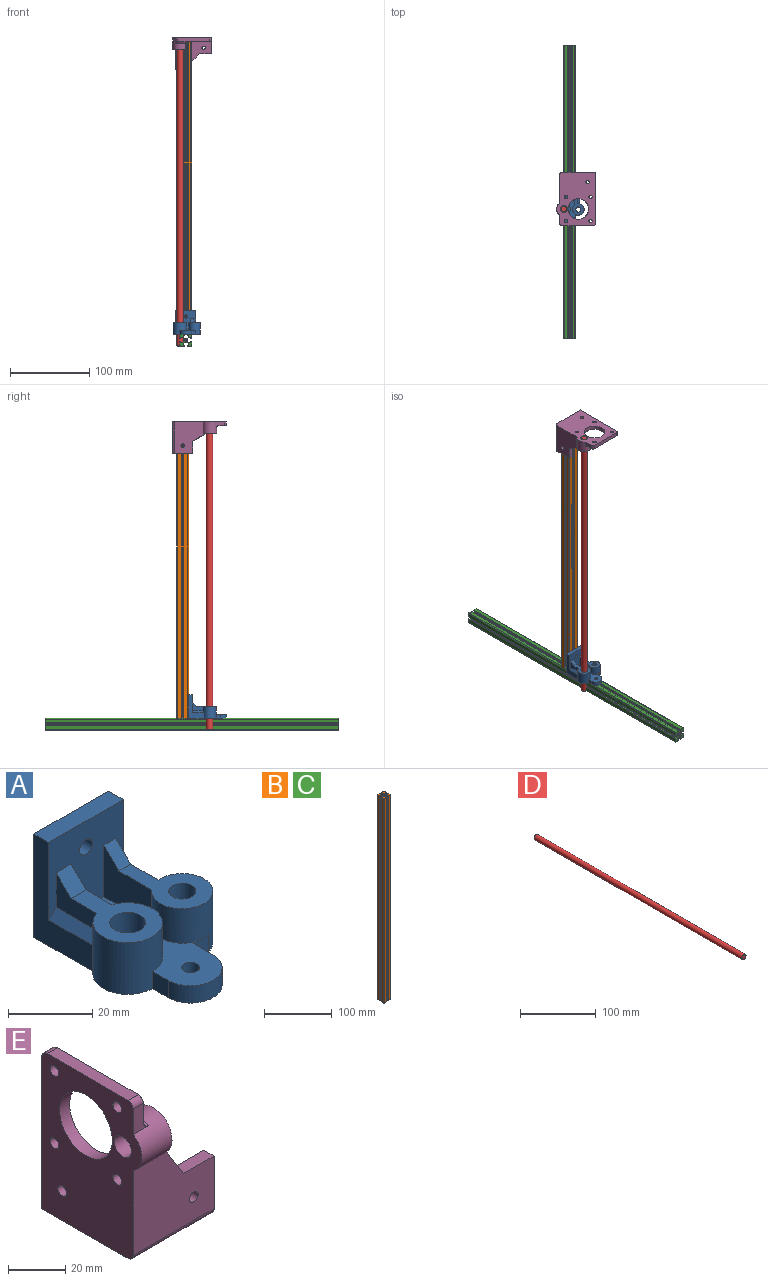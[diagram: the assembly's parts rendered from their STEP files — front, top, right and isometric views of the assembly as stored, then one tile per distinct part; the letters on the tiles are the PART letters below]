
ASSEMBLY  parts=5 mates=10
PART A: 29 faces, bbox 33.8x47.6x30 mm
  f0: plane 25x25mm, normal (0,-1,0), area 457.1mm2, adj f2,f7,f9,f16,f20,f21,f22,f23
  f1: cylinder r=8.25mm len=16.5mm, axis (0,0,-1), area 559.8mm2, adj f2,f9,f14,f15,f17,f21,f22,f26
  f2: plane 42.6x16.6mm, normal (0,0,1), area 386.9mm2, adj f0,f1,f3,f4,f5,f6,f10,f11
  f3: cylinder r=7.5mm len=15mm, axis (0,0,-1), area 117.8mm2, adj f2,f4,f14,f15
  f4: plane 6.55x5mm, normal (1,0,0), area 32.8mm2, adj f2,f3,f5,f15
  f5: plane 5x5mm, normal (0,-1,0), area 25mm2, adj f2,f4,f6,f15,f18
  f6: cylinder r=7.25mm len=15mm, axis (0,0,-1), area 498.4mm2, adj f2,f5,f7,f15,f18,f19,f23,f24
  f7: plane 30x19.45mm, normal (1,0,0), area 258.4mm2, adj f0,f6,f8,f15,f16,f25
  f8: plane 30x25mm, normal (0,1,0), area 735.8mm2, adj f7,f9,f15,f16,f20
  f9: plane 30x19.94mm, normal (-1,0,0), area 262mm2, adj f0,f1,f8,f15,f16,f26
  f10: cylinder r=2.12mm len=5mm, axis (0,0,-1), area 66.8mm2, adj f2,f15
  f11: cylinder r=2.12mm len=5mm, axis (0,0,-1), area 66.8mm2, adj f2,f15
  f12: cylinder r=4.25mm len=15mm, axis (0,0,-1), area 400.6mm2, adj f15,f17
  f13: cylinder r=3.25mm len=15mm, axis (0,0,-1), area 306.3mm2, adj f15,f19
  f14: plane 5.35x5mm, normal (-1,0,0), area 26.7mm2, adj f1,f2,f3,f15
  f15: plane 47.6x33.8mm, normal (0,0,-1), area 998.3mm2, adj f1,f3,f4,f5,f6,f7,f8,f9
  f16: plane 25x5mm, normal (0,0,1), area 125mm2, adj f0,f7,f8,f9
  f17: plane 24.75x16.5mm, normal (0,0,1), area 199mm2, adj f1,f12,f21,f22,f28
  f18: plane 3.4x0.2mm, normal (0,0,-1), area 0.5mm2, adj f5,f6
  f19: plane 23.75x14.5mm, normal (0,0,1), area 171.7mm2, adj f6,f13,f23,f24,f27
  f20: cylinder r=2.12mm len=5mm, axis (0,-1,0), area 66.8mm2, adj f0,f8
  f21: plane 15x13.64mm, normal (1,0,0), area 148.9mm2, adj f0,f1,f2,f17,f28
  f22: plane 13.64x10mm, normal (-1,0,0), area 80.7mm2, adj f0,f1,f17,f26,f28
  f23: plane 14.29x10mm, normal (1,0,0), area 84mm2, adj f0,f6,f19,f25,f27
  f24: plane 16.07x15mm, normal (-1,0,0), area 173.2mm2, adj f0,f2,f6,f19,f27
  f25: plane 14.47x2.52mm, normal (0.71,0,0.71), area 50.6mm2, adj f0,f6,f7,f23
  f26: plane 14.94x2.5mm, normal (-0.71,0,0.71), area 50.2mm2, adj f0,f1,f9,f22
  f27: plane 5x5mm, normal (0,-0.71,0.71), area 28.3mm2, adj f0,f19,f23,f24
  f28: plane 5x5mm, normal (0,-0.71,0.71), area 35.4mm2, adj f0,f17,f21,f22
PART B: 63 faces, bbox 15x15x370 mm
  f0: plane 370x4.8mm, normal (0,1,0), area 1776mm2, adj f1,f60,f61,f62
  f1: cylinder r=1mm len=370mm, axis (0,0,-1), area 581.2mm2, adj f0,f2,f61,f62
  f2: plane 370x4.8mm, normal (-1,0,0), area 1776mm2, adj f1,f3,f61,f62
  f3: plane 370x1.1mm, normal (0,-1,0), area 407mm2, adj f2,f4,f61,f62
  f4: plane 370x1.15mm, normal (1,0,0), area 425.5mm2, adj f3,f5,f61,f62
  f5: plane 370x2.6mm, normal (0,-1,0), area 962mm2, adj f4,f6,f61,f62
  f6: plane 370x1.15mm, normal (-0.75,-0.66,0), area 563.9mm2, adj f5,f7,f61,f62
  f7: plane 370x1.18mm, normal (-1,0,0), area 436.7mm2, adj f6,f8,f61,f62
  f8: plane 370x0.52mm, normal (-0.87,-0.5,0), area 222mm2, adj f7,f9,f61,f62
  f9: plane 370x0.52mm, normal (-0.87,0.5,0), area 222mm2, adj f8,f10,f61,f62
  f10: plane 370x1.18mm, normal (-1,0,0), area 436.7mm2, adj f9,f11,f61,f62
  f11: plane 370x1.15mm, normal (-0.75,0.66,0), area 563.9mm2, adj f10,f12,f61,f62
  f12: plane 370x2.6mm, normal (0,1,0), area 962mm2, adj f11,f13,f61,f62
  f13: plane 370x1.15mm, normal (1,0,0), area 425.5mm2, adj f12,f14,f61,f62
  f14: plane 370x1.1mm, normal (0,1,0), area 407mm2, adj f13,f15,f61,f62
  f15: plane 370x4.8mm, normal (-1,0,0), area 1776mm2, adj f14,f16,f61,f62
  f16: cylinder r=1mm len=370mm, axis (0,0,-1), area 581.2mm2, adj f15,f17,f61,f62
  f17: plane 370x4.8mm, normal (0,-1,0), area 1776mm2, adj f16,f18,f61,f62
  f18: plane 370x1.1mm, normal (1,0,0), area 407mm2, adj f17,f19,f61,f62
  f19: plane 370x1.15mm, normal (0,1,0), area 425.5mm2, adj f18,f20,f61,f62
  f20: plane 370x2.6mm, normal (1,0,0), area 962mm2, adj f19,f21,f61,f62
  f21: plane 370x1.15mm, normal (0.66,-0.75,0), area 563.9mm2, adj f20,f22,f61,f62
  f22: plane 370x1.18mm, normal (0,-1,0), area 436.7mm2, adj f21,f23,f61,f62
  f23: plane 370x0.52mm, normal (0.5,-0.87,0), area 222mm2, adj f22,f24,f61,f62
  f24: plane 370x0.52mm, normal (-0.5,-0.87,0), area 222mm2, adj f23,f25,f61,f62
  f25: plane 370x1.18mm, normal (0,-1,0), area 436.7mm2, adj f24,f26,f61,f62
  f26: plane 370x1.15mm, normal (-0.66,-0.75,0), area 563.9mm2, adj f25,f27,f61,f62
  f27: plane 370x2.6mm, normal (-1,0,0), area 962mm2, adj f26,f28,f61,f62
  f28: plane 370x1.15mm, normal (0,1,0), area 425.5mm2, adj f27,f29,f61,f62
  f29: plane 370x1.1mm, normal (-1,0,0), area 407mm2, adj f28,f30,f61,f62
  f30: plane 370x4.8mm, normal (0,-1,0), area 1776mm2, adj f29,f31,f61,f62
  f31: cylinder r=1mm len=370mm, axis (0,0,-1), area 581.2mm2, adj f30,f32,f61,f62
  f32: plane 370x4.8mm, normal (1,0,0), area 1776mm2, adj f31,f33,f61,f62
  f33: plane 370x1.1mm, normal (0,1,0), area 407mm2, adj f32,f34,f61,f62
  f34: plane 370x1.15mm, normal (-1,0,0), area 425.5mm2, adj f33,f35,f61,f62
  f35: plane 370x2.6mm, normal (0,1,0), area 962mm2, adj f34,f36,f61,f62
  f36: plane 370x1.15mm, normal (0.75,0.66,0), area 563.9mm2, adj f35,f37,f61,f62
  f37: plane 370x1.18mm, normal (1,0,0), area 436.7mm2, adj f36,f38,f61,f62
  f38: plane 370x0.52mm, normal (0.87,0.5,0), area 222mm2, adj f37,f39,f61,f62
  f39: plane 370x0.52mm, normal (0.87,-0.5,0), area 222mm2, adj f38,f40,f61,f62
  f40: plane 370x1.18mm, normal (1,0,0), area 436.7mm2, adj f39,f41,f61,f62
  f41: plane 370x1.15mm, normal (0.75,-0.66,0), area 563.9mm2, adj f40,f42,f61,f62
  f42: plane 370x2.6mm, normal (0,-1,0), area 962mm2, adj f41,f43,f61,f62
  f43: plane 370x1.15mm, normal (-1,0,0), area 425.5mm2, adj f42,f44,f61,f62
  f44: plane 370x1.1mm, normal (0,-1,0), area 407mm2, adj f43,f45,f61,f62
  f45: plane 370x4.8mm, normal (1,0,0), area 1776mm2, adj f44,f46,f61,f62
  f46: cylinder r=1mm len=370mm, axis (0,0,-1), area 581.2mm2, adj f45,f47,f61,f62
  f47: plane 370x4.8mm, normal (0,1,0), area 1776mm2, adj f46,f48,f61,f62
  f48: plane 370x1.1mm, normal (-1,0,0), area 407mm2, adj f47,f49,f61,f62
  f49: plane 370x1.15mm, normal (0,-1,0), area 425.5mm2, adj f48,f50,f61,f62
  f50: plane 370x2.6mm, normal (-1,0,0), area 962mm2, adj f49,f51,f61,f62
  f51: plane 370x1.15mm, normal (-0.66,0.75,0), area 563.9mm2, adj f50,f52,f61,f62
  f52: plane 370x1.18mm, normal (0,1,0), area 436.7mm2, adj f51,f53,f61,f62
  f53: plane 370x0.52mm, normal (-0.5,0.87,0), area 222mm2, adj f52,f54,f61,f62
  f54: plane 370x0.52mm, normal (0.5,0.87,0), area 222mm2, adj f53,f55,f61,f62
  f55: plane 370x1.18mm, normal (0,1,0), area 436.7mm2, adj f54,f56,f61,f62
  f56: plane 370x1.15mm, normal (0.66,0.75,0), area 563.9mm2, adj f55,f57,f61,f62
  f57: plane 370x2.6mm, normal (1,0,0), area 962mm2, adj f56,f58,f61,f62
  f58: plane 370x1.15mm, normal (0,-1,0), area 425.5mm2, adj f57,f60,f61,f62
  f59: cylinder r=1.25mm len=370mm, axis (0,0,-1), area 2906mm2, adj f61,f62
  f60: plane 370x1.1mm, normal (1,0,0), area 407mm2, adj f0,f58,f61,f62
  f61: plane 15x15mm, normal (0,0,1), area 126.2mm2, adj f0,f1,f2,f3,f4,f5,f6,f7
  f62: plane 15x15mm, normal (0,0,-1), area 126.2mm2, adj f0,f1,f2,f3,f4,f5,f6,f7
PART C: same geometry as B
PART D: 5 faces, bbox 8x390x8 mm
  f0: cylinder r=4mm len=389mm, axis (0,1,0), area 9776.6mm2, adj f3,f4
  f1: plane 7x7mm, normal (0,-1,0), area 38.5mm2, adj f4
  f2: plane 7x7mm, normal (0,1,0), area 38.5mm2, adj f3
  f3: cone r=4mm half-angle=45deg, axis (0,-1,0), area 16.7mm2, adj f0,f2
  f4: cone r=3.5mm half-angle=45deg, axis (0,1,0), area 16.7mm2, adj f0,f1
PART E: 36 faces, bbox 40x49.3x67.6 mm
  f0: plane 10.82x7.5mm, normal (0,-1,0), area 55.7mm2, adj f4,f11,f28,f30,f35
  f1: plane 35x23.9mm, normal (0,1,0), area 759.1mm2, adj f3,f4,f7,f15,f18,f31,f32
  f2: plane 14.94x7.9mm, normal (0,1,0), area 59.7mm2, adj f4,f5,f6,f31,f32,f34
  f3: plane 15x5mm, normal (0,0,1), area 75mm2, adj f1,f12,f15,f31
  f4: plane 62.6x45mm, normal (1,0,0), area 1806.8mm2, adj f0,f1,f2,f7,f10,f19,f20,f21
  f5: cylinder r=9.25mm len=7.5mm, axis (-1,0,0), area 58.1mm2, adj f2,f6,f23,f34
  f6: plane 18.5x16.12mm, normal (1,0,0), area 148.2mm2, adj f2,f5,f12,f23,f30,f31,f33
  f7: plane 40x35mm, normal (0,0,1), area 921.6mm2, adj f1,f4,f8,f9,f10,f13,f14,f15
  f8: plane 10x5mm, normal (0,1,0), area 50mm2, adj f7,f15,f16,f17
  f9: plane 15x5mm, normal (1,0,0), area 75mm2, adj f7,f10,f16,f17
  f10: plane 65.1x20mm, normal (0,1,0), area 400.5mm2, adj f4,f7,f9,f11,f16,f27
  f11: plane 67.6x49.25mm, normal (-1,0,0), area 2426mm2, adj f0,f10,f12,f16,f19,f20,f21,f22
  f12: plane 40x38.5mm, normal (0,-1,0), area 1171.6mm2, adj f3,f6,f11,f15,f18,f29,f30,f31
  f13: cylinder r=2.12mm len=5mm, axis (0,0,-1), area 66.8mm2, adj f7,f16
  f14: cylinder r=2.12mm len=5mm, axis (0,0,-1), area 66.8mm2, adj f7,f16
  f15: plane 25x20mm, normal (1,0,0), area 198.7mm2, adj f1,f3,f7,f8,f12,f16,f29
  f16: plane 42.5x40mm, normal (0,0,-1), area 1221.6mm2, adj f8,f9,f10,f11,f13,f14,f15,f17
  f17: plane 10x10mm, normal (0.71,0.71,0), area 70.7mm2, adj f7,f8,f9,f16
  f18: cylinder r=2.12mm len=5mm, axis (0,-1,0), area 66.8mm2, adj f1,f12
  f19: cylinder r=2.12mm len=5mm, axis (-1,0,0), area 66.8mm2, adj f4,f11
  f20: plane 40x5mm, normal (0,0,1), area 200mm2, adj f4,f11,f27,f28
  f21: cylinder r=2.12mm len=5mm, axis (-1,0,0), area 66.8mm2, adj f4,f11
  f22: cylinder r=4.25mm len=14.5mm, axis (-1,0,0), area 387.2mm2, adj f11,f33
  f23: cylinder r=13mm len=26mm, axis (-1,0,0), area 540.3mm2, adj f4,f5,f6,f11,f30,f34,f35
  f24: cylinder r=2.12mm len=5mm, axis (-1,0,0), area 66.8mm2, adj f4,f11
  f25: cylinder r=2.12mm len=5mm, axis (-1,0,0), area 66.8mm2, adj f4,f11
  f26: cylinder r=2.12mm len=5mm, axis (-1,0,0), area 66.8mm2, adj f4,f11
  f27: cylinder r=2.5mm len=5mm, axis (1,0,0), area 19.6mm2, adj f4,f10,f11,f20
  f28: cylinder r=2.5mm len=5mm, axis (-1,0,0), area 19.6mm2, adj f0,f4,f11,f20
  f29: cylinder r=2.5mm len=40mm, axis (1,0,0), area 157.1mm2, adj f11,f12,f15,f16
  f30: cylinder r=9.25mm len=17.03mm, axis (-1,0,0), area 375.1mm2, adj f0,f6,f11,f12,f23,f35
  f31: plane 16x10mm, normal (0.85,0,0.53), area 92mm2, adj f1,f2,f3,f6,f12,f32
  f32: cylinder r=3.5mm len=17.56mm, axis (-1,0,0), area 73.2mm2, adj f1,f2,f4,f31
  f33: cone r=4.25mm half-angle=45deg, axis (1,0,0), area 20mm2, adj f6,f22
  f34: torus R=11.75mm, axis (1,0,0), area 32.4mm2, adj f2,f4,f5,f23
  f35: torus R=11.75mm, axis (1,0,0), area 52.9mm2, adj f0,f4,f23,f30
PLACE A rot(axis=(-1,0,0),0deg) t=(-117.36,-78.12,35.78)mm
PLACE B rot(axis=(1,0,0),0deg) t=(-117.36,-44.12,220.78)mm
PLACE C rot(axis=(-1,0,0),90deg) t=(-117.36,-55.94,28.28)mm
PLACE D rot(axis=(1,0,0),90deg) t=(-124.86,-78.12,215.78)mm
PLACE E rot(axis=(0.58,0.58,-0.58),120deg) t=(-129.86,-31.62,390.78)mm
MATE planar B.f45 <-> C.f32  axis (1,0,0) through (-109.86,-40.02,220.78)mm
MATE planar E.f11 <-> D.f0  axis (0,0,1) through (-107.67,-62.39,410.78)mm
MATE cylindrical D.f0 <-> A.f1  axis (0,0,1) through (-124.86,-78.12,215.78)mm
MATE planar C.f17 <-> B.f59  axis (0,0,1) through (-121.46,-55.94,35.78)mm
MATE planar A.f15 <-> C.f30  axis (0,0,-1) through (-116.87,-72.51,35.78)mm
MATE planar C.f32 <-> A.f4  axis (1,0,0) through (-109.86,-55.94,32.38)mm
MATE planar E.f7 <-> B.f47  axis (0,-1,0) through (-108.98,-36.62,392.27)mm
MATE planar A.f8 <-> B.f17  axis (0,1,0) through (-117.36,-51.62,50.64)mm
MATE planar E.f1 <-> B.f15  axis (1,0,0) through (-124.86,-47.81,389.2)mm
MATE planar E.f24 <-> B.f61  axis (0,0,-1) through (-91.06,-62.62,405.78)mm
